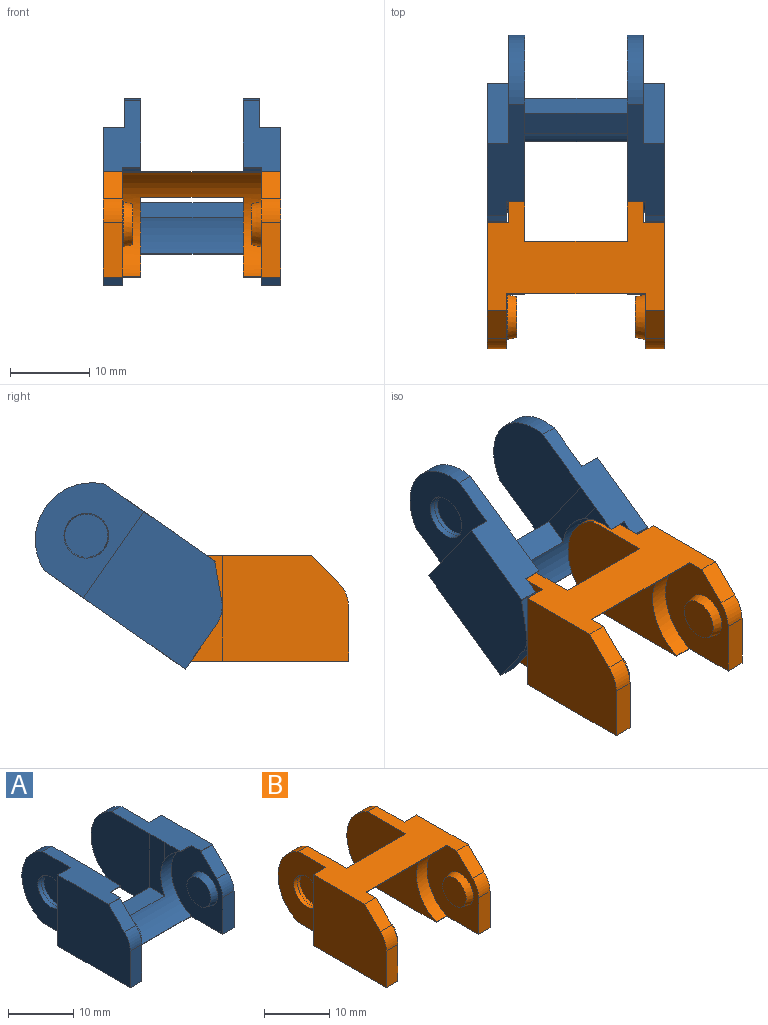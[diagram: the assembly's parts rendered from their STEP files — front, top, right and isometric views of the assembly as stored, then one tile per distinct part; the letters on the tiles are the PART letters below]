
ASSEMBLY  parts=2 mates=1
PART A: 54 faces, bbox 22.4x26.2x13.3 mm
  f0: plane 22.44x21.72mm, normal (0,0,-1), area 228.5mm2, adj f3,f4,f5,f6,f7,f11,f12,f13
  f1: plane 17.07x4.77mm, normal (0,0,1), area 60.1mm2, adj f6,f11,f14,f15,f18,f25,f26,f29
  f2: plane 17.07x4.77mm, normal (0,0,1), area 60.1mm2, adj f3,f5,f11,f12,f13,f19,f20,f21
  f3: plane 13.3x11.08mm, normal (-1,0,0), area 93.4mm2, adj f0,f2,f4,f11,f17,f48,f49,f50
  f4: cylinder r=7.2mm len=1.12mm, axis (-1,0,0), area 0mm2, adj f0,f3,f23,f51
  f5: plane 15.67x13.3mm, normal (1,0,0), area 196.6mm2, adj f0,f2,f48,f49,f50,f51,f53
  f6: plane 13.3x11.08mm, normal (1,0,0), area 93.7mm2, adj f0,f1,f11,f30,f31,f44,f45,f46
  f7: plane 12.89x3.28mm, normal (0,1,0), area 42.3mm2, adj f0,f13,f14,f43
  f8: plane 12.7x0.01mm, normal (0,-1,0), area 0.1mm2, adj f9,f10,f11,f43
  f9: cone r=7.2mm half-angle=87.6deg, axis (1,0,0), area 0mm2, adj f8,f11,f43
  f10: cone r=7.2mm half-angle=87.6deg, axis (-1,0,0), area 0mm2, adj f8,f11,f43
  f11: cylinder r=7.2mm len=17.49mm, axis (-1,0,0), area 138.2mm2, adj f0,f1,f2,f3,f6,f8,f9,f10
  f12: plane 13.3x10.49mm, normal (1,0,0), area 94.9mm2, adj f0,f2,f35,f40,f53
  f13: plane 13.3x12.74mm, normal (-1,0,0), area 153.1mm2, adj f0,f2,f7,f35,f42
  f14: plane 13.3x12.74mm, normal (1,0,0), area 153.1mm2, adj f0,f1,f7,f34,f41
  f15: plane 13.3x10.49mm, normal (-1,0,0), area 98mm2, adj f0,f1,f34,f38,f52
  f16: plane 5.13x5.13mm, normal (-1,0,0), area 20.7mm2, adj f17
  f17: cone r=2.56mm half-angle=12.7deg, axis (1,0,0), area 22.1mm2, adj f3,f16
  f18: plane 15.67x13.3mm, normal (-1,0,0), area 196.6mm2, adj f0,f1,f44,f45,f46,f47,f52
  f19: plane 0.16x0.07mm, normal (-1,0,0), area 0mm2, adj f2,f11,f20
  f20: plane 2.29x0.07mm, normal (0,-1,0), area 0.2mm2, adj f2,f11,f19,f21
  f21: plane 3.44x3.27mm, normal (-1,0,0), area 4.5mm2, adj f2,f11,f20,f42
  f22: plane 0.16x0.07mm, normal (-1,0,0), area 0mm2, adj f0,f11,f24
  f23: plane 1.12x0.58mm, normal (-1,0,0), area 0.3mm2, adj f0,f4,f51
  f24: plane 17.46x0.07mm, normal (0,-1,0), area 1.2mm2, adj f0,f11,f22,f28
  f25: plane 3.44x3.27mm, normal (1,0,0), area 4.5mm2, adj f1,f11,f26,f41
  f26: plane 2.29x0.07mm, normal (0,-1,0), area 0.2mm2, adj f1,f11,f25,f29
  f27: plane 1.12x0.58mm, normal (1,0,0), area 0.3mm2, adj f0,f30,f44
  f28: plane 0.16x0.07mm, normal (1,0,0), area 0mm2, adj f0,f11,f24
  f29: plane 0.16x0.07mm, normal (1,0,0), area 0mm2, adj f1,f11,f26
  f30: cylinder r=7.2mm len=1.12mm, axis (-1,0,0), area 0mm2, adj f0,f6,f27,f44
  f31: cylinder r=2.83mm len=5.66mm, axis (-1,0,0), area 1.6mm2, adj f6,f33
  f32: plane 5.13x5.13mm, normal (1,0,0), area 20.7mm2, adj f33
  f33: cone r=2.56mm half-angle=12.7deg, axis (-1,0,0), area 20.4mm2, adj f31,f32
  f34: cylinder r=7.2mm len=13.3mm, axis (1,0,0), area 34.7mm2, adj f0,f1,f14,f15
  f35: cylinder r=7.2mm len=13.3mm, axis (1,0,0), area 34.7mm2, adj f0,f2,f12,f13
  f36: plane 5.45x5.45mm, normal (-1,0,0), area 23.3mm2, adj f37
  f37: cone r=2.76mm half-angle=12.7deg, axis (-1,0,0), area 8.3mm2, adj f36,f38
  f38: cylinder r=2.83mm len=5.66mm, axis (-1,0,0), area 13.3mm2, adj f15,f37
  f39: plane 5.45x5.45mm, normal (1,0,0), area 23.3mm2, adj f40
  f40: cone r=2.76mm half-angle=12.7deg, axis (1,0,0), area 22.4mm2, adj f12,f39
  f41: plane 10.02x3.18mm, normal (1,0,0), area 28mm2, adj f1,f11,f14,f25,f43
  f42: plane 10.02x3.18mm, normal (-1,0,0), area 28mm2, adj f2,f11,f13,f21,f43
  f43: plane 12.89x3.18mm, normal (0,0,1), area 41mm2, adj f7,f8,f9,f10,f11,f41,f42
  f44: plane 6.88x2.49mm, normal (0,-1,0), area 17mm2, adj f0,f6,f18,f27,f30,f47
  f45: plane 2.47x0.07mm, normal (0,-0.71,-0.71), area 0.2mm2, adj f1,f6,f18,f46
  f46: plane 3.44x3.43mm, normal (0,-0.71,0.71), area 12mm2, adj f6,f18,f45,f47
  f47: cylinder r=4.03mm len=2.92mm, axis (-1,0,0), area 8.1mm2, adj f6,f18,f44,f46
  f48: plane 2.47x0.07mm, normal (0,-0.71,-0.71), area 0.2mm2, adj f2,f3,f5,f49
  f49: plane 3.44x3.43mm, normal (0,-0.71,0.71), area 12mm2, adj f3,f5,f48,f50
  f50: cylinder r=4.03mm len=2.92mm, axis (-1,0,0), area 8.1mm2, adj f3,f5,f49,f51
  f51: plane 6.88x2.49mm, normal (0,-1,0), area 17mm2, adj f0,f3,f4,f5,f23,f50
  f52: plane 13.3x2.73mm, normal (0,1,0), area 36.3mm2, adj f0,f1,f15,f18
  f53: plane 13.3x2.73mm, normal (0,1,0), area 36.3mm2, adj f0,f2,f5,f12
PART B: 39 faces, bbox 22.4x26.3x13.3 mm
  f0: plane 21.82x4.77mm, normal (0,0,-1), area 72.1mm2, adj f1,f7,f8,f15,f17,f23,f27,f31
  f1: plane 6.88x2.47mm, normal (0,-1,0), area 17mm2, adj f0,f17,f19,f27
  f2: plane 21.82x4.77mm, normal (0,0,-1), area 72.1mm2, adj f4,f5,f6,f12,f13,f16,f26,f32
  f3: cylinder r=7.2mm len=17.49mm, axis (-1,0,0), area 137.7mm2, adj f4,f6,f7,f9,f12,f22,f23,f24
  f4: plane 2.3x0.07mm, normal (0,-1,0), area 0.2mm2, adj f2,f3,f6,f12
  f5: plane 13.3x10.39mm, normal (1,0,0), area 93.6mm2, adj f2,f9,f13,f32,f37
  f6: plane 19.36x13.3mm, normal (-1,0,0), area 185.8mm2, adj f2,f3,f4,f9,f14,f32,f38
  f7: plane 19.36x13.3mm, normal (1,0,0), area 185.8mm2, adj f0,f3,f9,f14,f23,f31,f38
  f8: plane 13.3x10.39mm, normal (-1,0,0), area 96.7mm2, adj f0,f9,f15,f31,f35
  f9: plane 22.44x17.07mm, normal (0,0,1), area 206mm2, adj f3,f5,f6,f7,f8,f12,f13,f14
  f10: plane 5.13x5.13mm, normal (-1,0,0), area 20.7mm2, adj f11
  f11: cone r=2.56mm half-angle=12.7deg, axis (1,0,0), area 22.1mm2, adj f10,f12
  f12: plane 13.3x11.18mm, normal (-1,0,0), area 95.2mm2, adj f2,f3,f4,f9,f11,f20,f21,f26
  f13: plane 13.3x2.73mm, normal (0,1,0), area 36.3mm2, adj f2,f5,f9,f16
  f14: plane 12.89x3.24mm, normal (0,1,0), area 41.8mm2, adj f6,f7,f9,f38
  f15: plane 13.3x2.73mm, normal (0,1,0), area 36.3mm2, adj f0,f8,f9,f17
  f16: plane 15.87x13.3mm, normal (1,0,0), area 199.5mm2, adj f2,f9,f13,f20,f21,f26
  f17: plane 15.87x13.3mm, normal (-1,0,0), area 199.5mm2, adj f0,f1,f9,f15,f18,f19
  f18: plane 3.44x3.43mm, normal (0,-0.71,0.71), area 12mm2, adj f9,f17,f19,f27
  f19: cylinder r=4.13mm len=2.99mm, axis (-1,0,0), area 8.3mm2, adj f1,f17,f18,f27
  f20: plane 3.44x3.43mm, normal (0,-0.71,0.71), area 12mm2, adj f9,f12,f16,f21
  f21: cylinder r=4.13mm len=2.99mm, axis (-1,0,0), area 8.3mm2, adj f12,f16,f20,f26
  f22: plane 0.16x0.07mm, normal (-1,0,0), area 0mm2, adj f3,f9,f24
  f23: plane 2.3x0.07mm, normal (0,-1,0), area 0.2mm2, adj f0,f3,f7,f27
  f24: plane 17.46x0.07mm, normal (0,-1,0), area 1.2mm2, adj f3,f9,f22,f25
  f25: plane 0.16x0.07mm, normal (1,0,0), area 0mm2, adj f3,f9,f24
  f26: plane 6.88x2.47mm, normal (0,-1,0), area 17mm2, adj f2,f12,f16,f21
  f27: plane 13.3x11.18mm, normal (1,0,0), area 95.5mm2, adj f0,f1,f3,f9,f18,f19,f23,f28
  f28: cylinder r=2.83mm len=5.66mm, axis (-1,0,0), area 1.6mm2, adj f27,f30
  f29: plane 5.13x5.13mm, normal (1,0,0), area 20.7mm2, adj f30
  f30: cone r=2.56mm half-angle=12.7deg, axis (-1,0,0), area 20.4mm2, adj f28,f29
  f31: cylinder r=7.2mm len=13.3mm, axis (1,0,0), area 34.7mm2, adj f0,f7,f8,f9
  f32: cylinder r=7.2mm len=13.3mm, axis (1,0,0), area 34.7mm2, adj f2,f5,f6,f9
  f33: plane 5.45x5.45mm, normal (-1,0,0), area 23.3mm2, adj f34
  f34: cone r=2.76mm half-angle=12.7deg, axis (-1,0,0), area 8.3mm2, adj f33,f35
  f35: cylinder r=2.83mm len=5.66mm, axis (-1,0,0), area 13.3mm2, adj f8,f34
  f36: plane 5.45x5.45mm, normal (1,0,0), area 23.3mm2, adj f37
  f37: cone r=2.76mm half-angle=12.7deg, axis (1,0,0), area 22.4mm2, adj f5,f36
  f38: plane 12.89x3.2mm, normal (0,0,-1), area 41.2mm2, adj f3,f6,f7,f14
PLACE A rot(axis=(1,0,0),35deg) t=(-0.39,15.04,7.64)mm
PLACE B t=(-0.39,0.7,2.39)mm fixed
MATE revolute A.f4 <-> B.f34  axis (-1,0,0) through (7.09,7.54,2.39)mm
